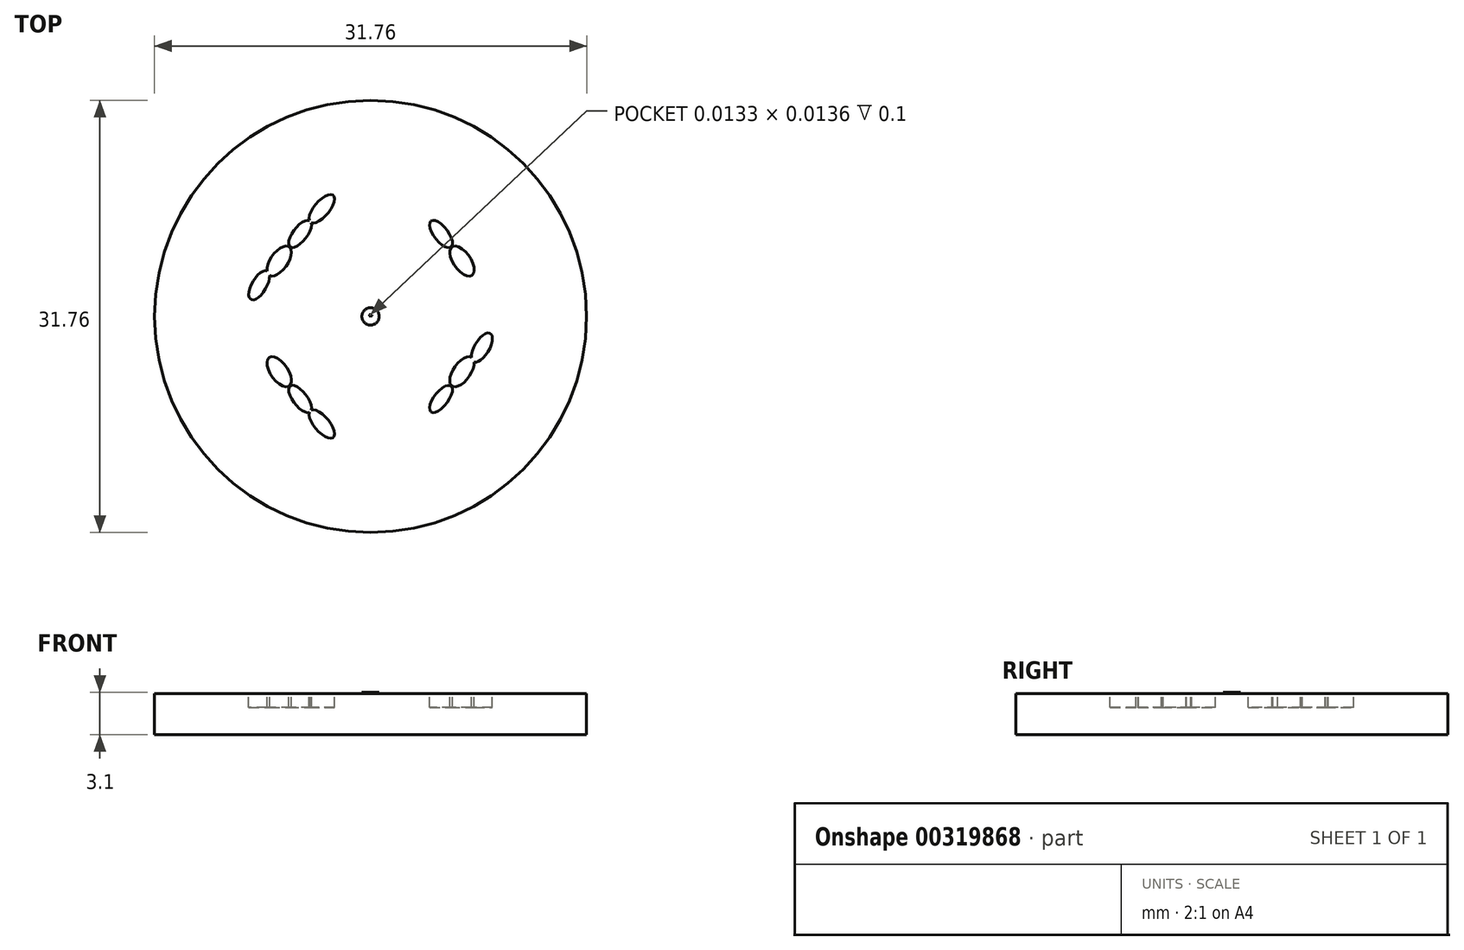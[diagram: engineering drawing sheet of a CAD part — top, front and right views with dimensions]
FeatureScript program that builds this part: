
annotation { "Feature Type Name" : "Feature", "Feature Type Description" : "" }
export const myFeature = defineFeature(function(context is Context, id is Id, definition is map)
    precondition{}
    {
        {
            var Q0;
            Q0=qCreatedBy(makeId("Top.planeOp"),FACE);
            var sketch = newSketch(context, id + "F0", { "sketchPlane" : qUnion([Q0])});
            skCircle(sketch, "E0", {"center": v(0, 0) * mm, "radius": 15.88 * mm});
            skSolve(sketch);
        }
        {
            var Q0;
            Q0 = qSketchRegion(id + "F0", true);
            extrude(context, id + "F1", {"entities" : qUnion([Q0]), "depth" : 3 * mm});
        }
        {
            var Q0;
            Q0=makeQuery(id+"F1.opExtrude","CAP_FACE",FACE,{"disambiguationData":[OSD([sQuery(id+"F0.wireOp",EDGE,"E0")])],"isStart":false});
            var sketch = newSketch(context, id + "F2", { "sketchPlane" : qUnion([Q0])});
            skEllipse(sketch, "E1", {"center": v(-8.19, 2.3) * mm, "majorRadius": 1.2 * mm, "minorRadius": 0.54 * mm, "majorAxis": v(0.5, 0.86)});
            skEllipse(sketch, "E2", {"center": v(-6.72, 4.07) * mm, "majorRadius": 1.27 * mm, "minorRadius": 0.63 * mm, "majorAxis": v(-0.58, -0.82)});
            skEllipse(sketch, "E3", {"center": v(-5.18, 6.06) * mm, "majorRadius": 1.2 * mm, "minorRadius": 0.52 * mm, "majorAxis": v(0.61, 0.8)});
            skEllipse(sketch, "E4", {"center": v(-3.58, 7.9) * mm, "majorRadius": 1.29 * mm, "minorRadius": 0.56 * mm, "majorAxis": v(-0.64, -0.76)});
            skEllipse(sketch, "E5.MirrorC", {"center": v(-5.18, -6.06) * mm, "majorRadius": 1.2 * mm, "minorRadius": 0.52 * mm, "majorAxis": v(0.61, -0.8)});
            skEllipse(sketch, "E6.MirrorC", {"center": v(-3.58, -7.9) * mm, "majorRadius": 1.29 * mm, "minorRadius": 0.56 * mm, "majorAxis": v(-0.64, 0.76)});
            skEllipse(sketch, "E7.MirrorC", {"center": v(-6.72, -4.07) * mm, "majorRadius": 1.27 * mm, "minorRadius": 0.63 * mm, "majorAxis": v(-0.58, 0.82)});
            skEllipse(sketch, "E8.MirrorC", {"center": v(6.72, 4.07) * mm, "majorRadius": 1.27 * mm, "minorRadius": 0.63 * mm, "majorAxis": v(0.58, -0.82)});
            skEllipse(sketch, "E9.MirrorC", {"center": v(6.72, -4.07) * mm, "majorRadius": 1.27 * mm, "minorRadius": 0.63 * mm, "majorAxis": v(0.58, 0.82)});
            skEllipse(sketch, "E10.MirrorC", {"center": v(8.19, -2.3) * mm, "majorRadius": 1.2 * mm, "minorRadius": 0.54 * mm, "majorAxis": v(-0.5, -0.86)});
            skEllipse(sketch, "E11.MirrorC", {"center": v(5.18, 6.06) * mm, "majorRadius": 1.2 * mm, "minorRadius": 0.52 * mm, "majorAxis": v(-0.61, 0.8)});
            skEllipse(sketch, "E12.MirrorC", {"center": v(5.18, -6.06) * mm, "majorRadius": 1.2 * mm, "minorRadius": 0.52 * mm, "majorAxis": v(-0.61, -0.8)});
            skSolve(sketch);
        }
        {
            var Q0;
            Q0 = qSketchRegion(id + "F2", true);
            extrude(context, id + "F3", {"entities" : qUnion([Q0]), "operationType" : NewBodyOperationType.REMOVE, "oppositeDirection" : true, "depth" : 1 * mm});
        }
        {
            var Q0;
            Q0=makeQuery(id+"F1.opExtrude","CAP_FACE",FACE,{"disambiguationData":[OSD([sQuery(id+"F0.wireOp",EDGE,"E0")])],"isStart":false});
            var sketch = newSketch(context, id + "F4", { "sketchPlane" : qUnion([Q0])});
            skCircle(sketch, "E13", {"center": v(0, 0) * mm, "radius": 0.64 * mm});
            skText(sketch, "E14", { "text": "life", "fontName": "RobotoSlab-Regular.ttf"});
            const initialGuessF4  = {"E14": [-0.0001, 3e-05, 1, 0, 0.0001]};
            skSetInitialGuess(sketch, initialGuessF4);
            skSolve(sketch);
        }
        {
            var Q0;
            Q0 = qSketchRegion(id + "F4", true);
            extrude(context, id + "F5", {"entities" : qUnion([Q0]), "operationType" : NewBodyOperationType.ADD, "depth" : .1 * mm});
        }
    });
